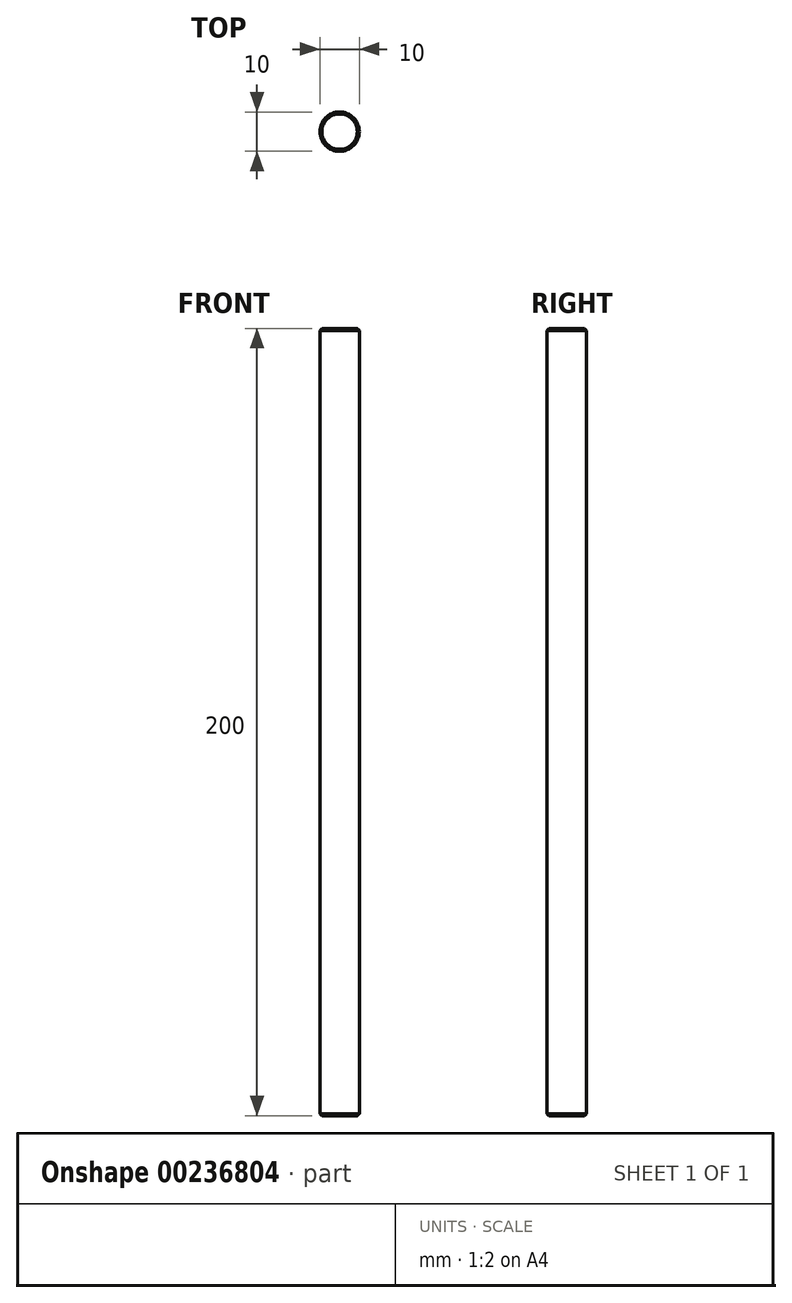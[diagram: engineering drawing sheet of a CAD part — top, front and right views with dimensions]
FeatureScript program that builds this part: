
annotation { "Feature Type Name" : "Feature", "Feature Type Description" : "" }
export const myFeature = defineFeature(function(context is Context, id is Id, definition is map)
    precondition{}
    {
        {
            var Q0;
            Q0=qCreatedBy(makeId("Top.planeOp"),FACE);
            var sketch = newSketch(context, id + "F0", { "sketchPlane" : qUnion([Q0])});
            skCircle(sketch, "E0", {"center": v(0, 0) * mm, "radius": 5 * mm});
            skSolve(sketch);
        }
        {
            var Q0;
            Q0 = qSketchRegion(id + "F0", true);
            extrude(context, id + "F1", {"entities" : qUnion([Q0]), "depth" : 200 * mm, "offsetDistance" : 25 * mm});
        }
        {
            var Q0;
            Q0=makeQuery(id+"F1.opExtrude","CAP_EDGE",EDGE,{"disambiguationData":[OSD([sQuery(id+"F0.wireOp",EDGE,"E0")])],"isStart":false});
            var Q1;
            Q1=makeQuery(id+"F1.opExtrude","CAP_EDGE",EDGE,{"disambiguationData":[OSD([sQuery(id+"F0.wireOp",EDGE,"E0")])],"isStart":true});
            chamfer(context, id + "F2", {"entities" : qUnion([Q0, Q1]), "width" : .5 * mm, "tangentPropagation" : true});
        }
    });
